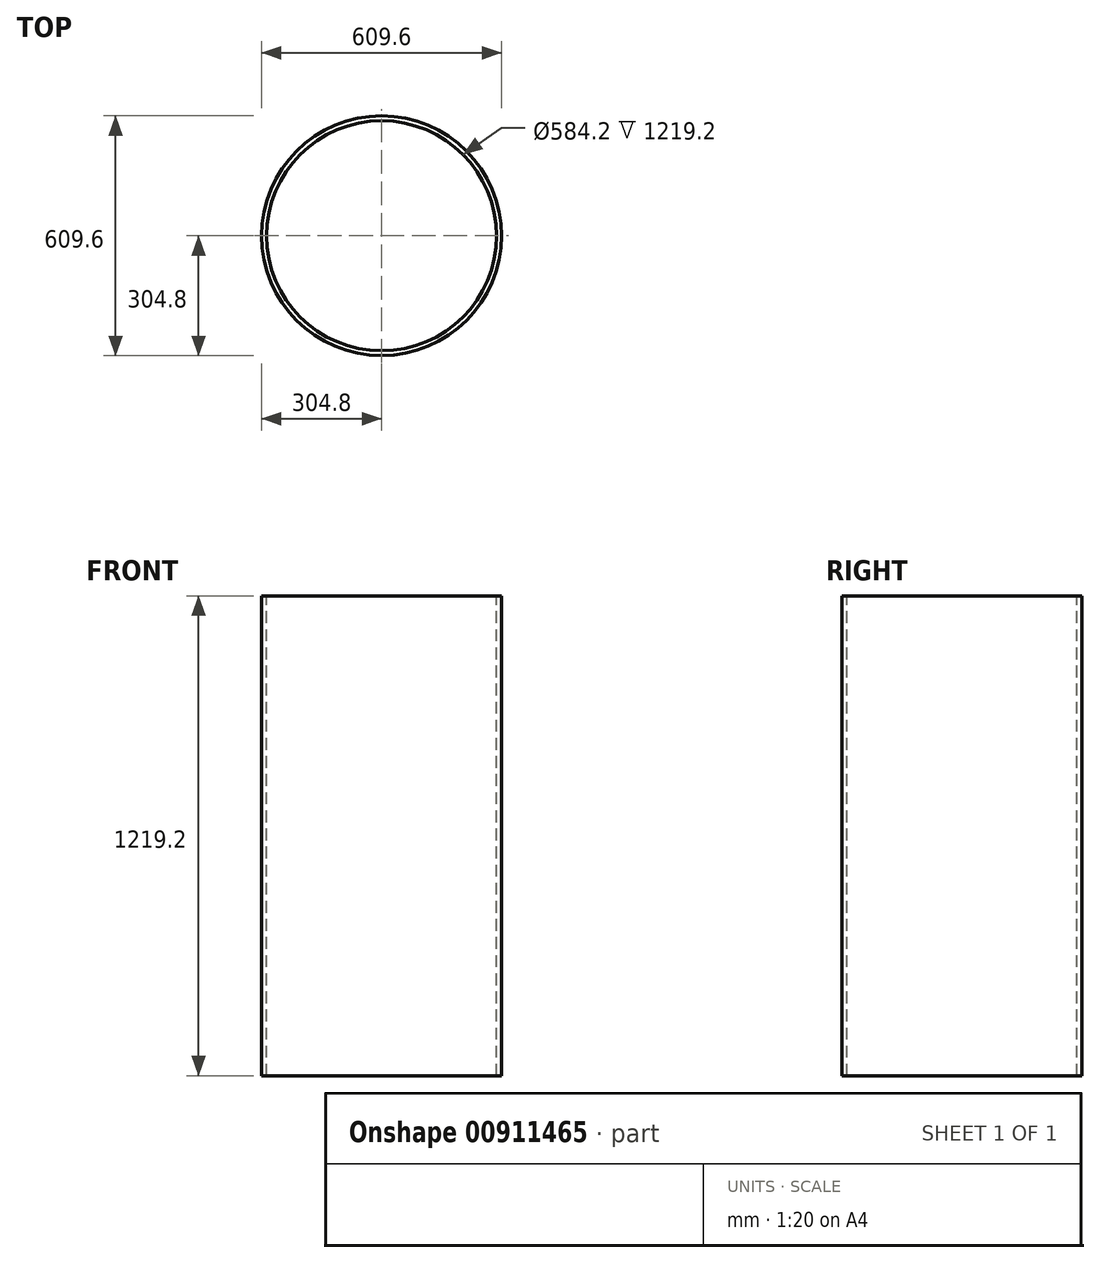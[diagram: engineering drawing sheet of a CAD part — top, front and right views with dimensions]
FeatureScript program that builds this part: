
annotation { "Feature Type Name" : "Feature", "Feature Type Description" : "" }
export const myFeature = defineFeature(function(context is Context, id is Id, definition is map)
    precondition{}
    {
        {
            var Q0;
            Q0=qCreatedBy(makeId("Top.planeOp"),FACE);
            var sketch = newSketch(context, id + "F0", { "sketchPlane" : qUnion([Q0])});
            skCircle(sketch, "E0", {"center": v(0, 0) * mm, "radius": 304.8 * mm});
            skSolve(sketch);
        }
        {
            var Q0;
            Q0=makeQuery(id+"F0.imprint","IMPRINT",FACE,{"disambiguationData":[TD([[makeQuery(id+"F0.imprint","IMPRINT",EDGE,{"derivedFrom":sQuery(id+"F0.wireOp",EDGE,"E0")}),1.0]])]});
            extrude(context, id + "F1", {"entities" : qUnion([Q0]), "oppositeDirection" : true, "depth" : 1219.2 * mm, "offsetDistance" : 25.4 * mm});
        }
        {
            var Q0;
            Q0=makeQuery(id+"F1.opExtrude","CAP_FACE",FACE,{"disambiguationData":[OSD([sQuery(id+"F0.wireOp",EDGE,"E0")])],"isStart":true});
            var Q1;
            Q1=makeQuery(id+"F1.opExtrude","CAP_FACE",FACE,{"disambiguationData":[OSD([sQuery(id+"F0.wireOp",EDGE,"E0")])],"isStart":false});
            shell(context, id + "F2", {"entities" : qUnion([Q0, Q1]), "thickness" : 12.7 * mm});
        }
    });
